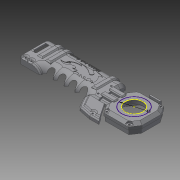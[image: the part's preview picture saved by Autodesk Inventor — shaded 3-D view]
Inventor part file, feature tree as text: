
AUTODESK INVENTOR PART (.ipt)
format: ipt  version: 2018 (Build 220112000, 112)  size: 1,809,408 bytes
history: native  units: mm
features: extrude x5, sketch x5, other x2, projected_geometry x2, mirror x1, fillet x1
ambient origin geometry x8: Origin, YZ Plane, XZ Plane, XY Plane, X Axis, Y Axis, Z Axis, Center Point
bodies: Body1 (feature_tree)
feature tree (16):
  other  "ソリッド2"
  extrude  "押し出し1"  Depth=10.0mm TaperAngle=0.0deg
  mirror  "ミラー1"
  extrude  "押し出し2"  Depth=10.0mm TaperAngle=0.0deg
  extrude  "押し出し3"  Depth=5.0mm TaperAngle=0.0deg
  extrude  "押し出し4"  Depth=2.5mm TaperAngle=0.0deg
  fillet  "フィレット1"  Radius=1.0mm
  extrude  "押し出し5"  Depth=2.0mm
  sketch  "スケッチ1"
  projected_geometry  "投影ループ1"
  sketch  "スケッチ2"
  sketch  "スケッチ3"
  projected_geometry  "投影ループ2"
  sketch  "スケッチ4"
  sketch  "スケッチ5"
  other  "ソリッド1"
